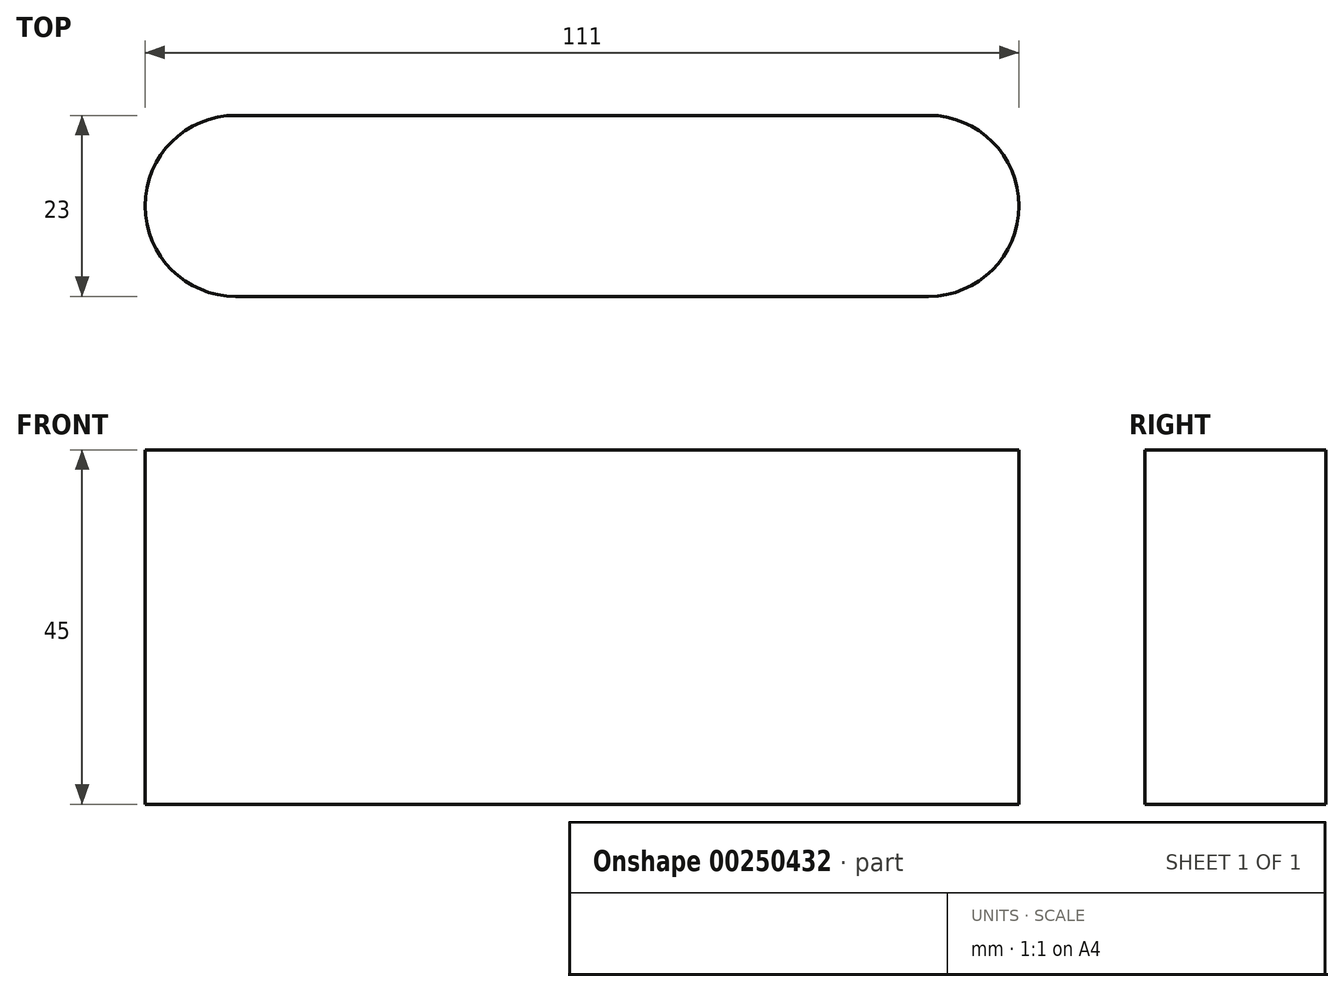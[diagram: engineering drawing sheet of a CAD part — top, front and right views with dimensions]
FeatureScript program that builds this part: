
annotation { "Feature Type Name" : "Feature", "Feature Type Description" : "" }
export const myFeature = defineFeature(function(context is Context, id is Id, definition is map)
    precondition{}
    {
        {
            var Q0;
            Q0=qCreatedBy(makeId("Front.planeOp"),FACE);
            var sketch = newSketch(context, id + "F0", { "sketchPlane" : qUnion([Q0])});
            skLineSegment(sketch, "E0.bottom", {"start": v(55.5, -22.5) * mm, "end": v(-55.5, -22.5) * mm});
            skLineSegment(sketch, "E0.top", {"start": v(55.5, 22.5) * mm, "end": v(-55.5, 22.5) * mm});
            skLineSegment(sketch, "E0.left", {"start": v(55.5, -22.5) * mm, "end": v(55.5, 22.5) * mm});
            skLineSegment(sketch, "E0.right", {"start": v(-55.5, -22.5) * mm, "end": v(-55.5, 22.5) * mm});
            skPoint(sketch, "E0.middle", {"position": v(0, 0) * mm});
            skSolve(sketch);
        }
        {
            var Q0;
            Q0=makeQuery(id+"F0.imprint","IMPRINT",FACE,{"disambiguationData":[TD([[makeQuery(id+"F0.imprint","IMPRINT",EDGE,{"derivedFrom":sQuery(id+"F0.wireOp",EDGE,"E0.bottom")}),-1.0]])]});
            extrude(context, id + "F1", {"entities" : qUnion([Q0]), "endBound" : BoundingType.SYMMETRIC, "depth" : 23 * mm});
        }
        {
            var Q0;
            Q0=makeQuery(id+"F1.opExtrude","CAP_EDGE",EDGE,{"disambiguationData":[OSD([sQuery(id+"F0.wireOp",EDGE,"E0.right")])],"isStart":false});
            var Q1;
            Q1=makeQuery(id+"F1.opExtrude","CAP_EDGE",EDGE,{"disambiguationData":[OSD([sQuery(id+"F0.wireOp",EDGE,"E0.right")])],"isStart":true});
            var Q2;
            Q2=makeQuery(id+"F1.opExtrude","CAP_EDGE",EDGE,{"disambiguationData":[OSD([sQuery(id+"F0.wireOp",EDGE,"E0.left")])],"isStart":true});
            var Q3;
            Q3=makeQuery(id+"F1.opExtrude","CAP_EDGE",EDGE,{"disambiguationData":[OSD([sQuery(id+"F0.wireOp",EDGE,"E0.left")])],"isStart":false});
            fillet(context, id + "F2", {"entities" : qUnion([Q0, Q1, Q2, Q3]), "radius" : 11.5 * mm, "tangentPropagation" : true, "allowEdgeOverflow" : false});
        }
    });
